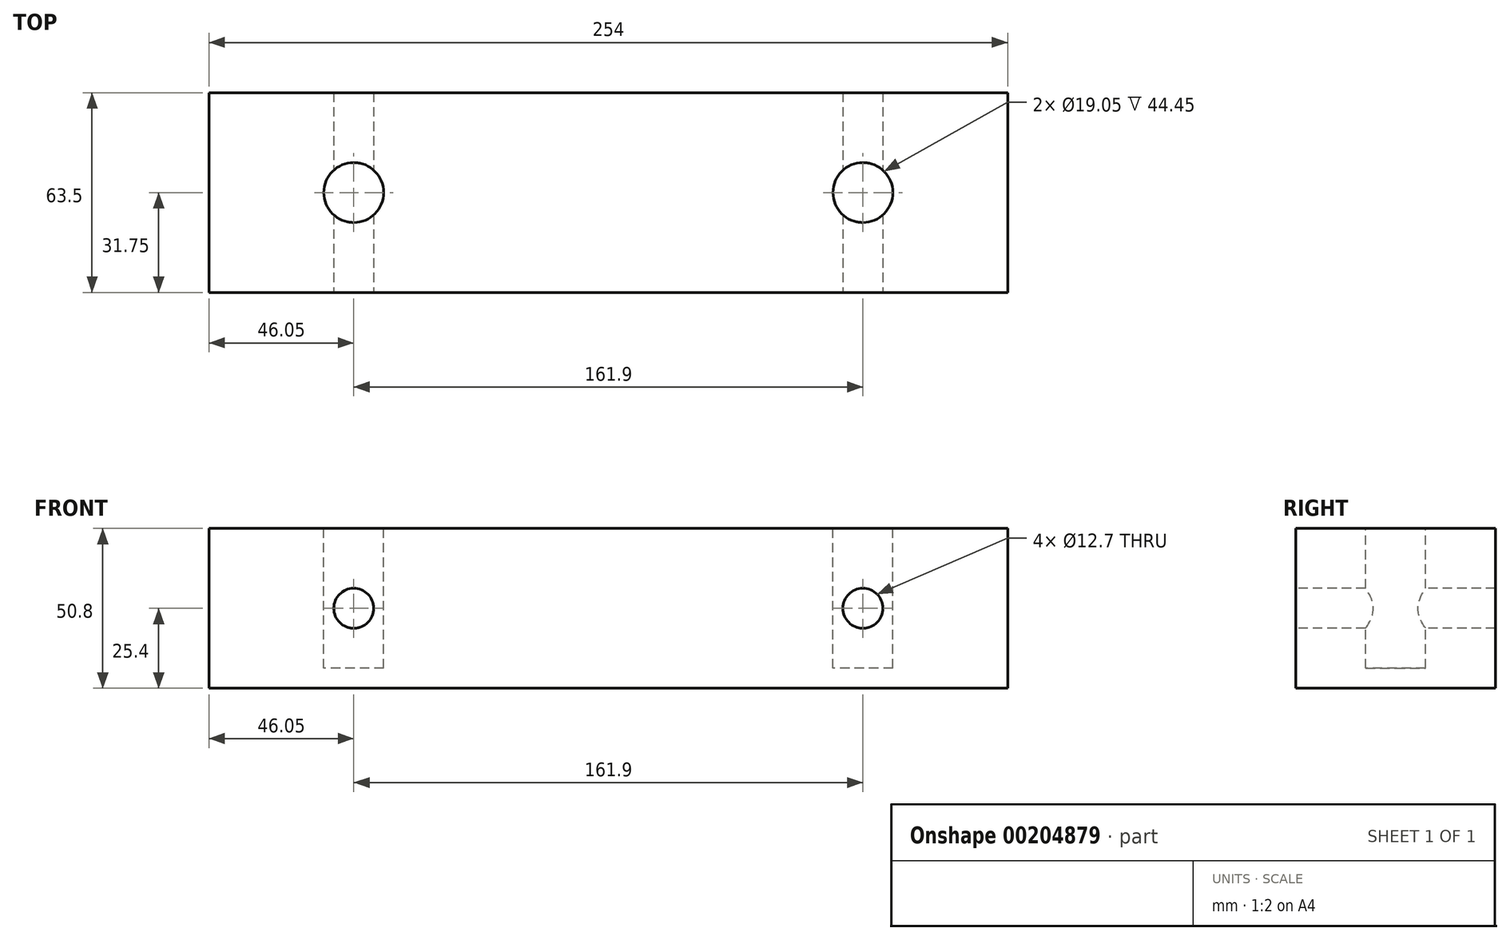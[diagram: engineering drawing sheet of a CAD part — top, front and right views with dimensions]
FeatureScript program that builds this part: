
annotation { "Feature Type Name" : "Feature", "Feature Type Description" : "" }
export const myFeature = defineFeature(function(context is Context, id is Id, definition is map)
    precondition{}
    {
        {
            var Q0;
            Q0=qCreatedBy(makeId("Front.planeOp"),FACE);
            var sketch = newSketch(context, id + "F0", { "sketchPlane" : qUnion([Q0])});
            skLineSegment(sketch, "E0.bottom", {"start": v(-127, -25.4) * mm, "end": v(127, -25.4) * mm});
            skLineSegment(sketch, "E0.top", {"start": v(-127, 25.4) * mm, "end": v(127, 25.4) * mm});
            skLineSegment(sketch, "E0.left", {"start": v(-127, -25.4) * mm, "end": v(-127, 25.4) * mm});
            skLineSegment(sketch, "E0.right", {"start": v(127, -25.4) * mm, "end": v(127, 25.4) * mm});
            skSolve(sketch);
        }
        {
            var Q0;
            Q0=makeQuery(id+"F0.imprint","IMPRINT",FACE,{"disambiguationData":[TD([[makeQuery(id+"F0.imprint","IMPRINT",EDGE,{"derivedFrom":sQuery(id+"F0.wireOp",EDGE,"E0.bottom")}),1.0]])]});
            extrude(context, id + "F1", {"entities" : qUnion([Q0]), "endBound" : BoundingType.SYMMETRIC, "depth" : 63.5 * mm});
        }
        {
            var Q0;
            Q0=makeQuery(id+"F1.opExtrude","SWEPT_FACE",FACE,{"disambiguationData":[OSD([sQuery(id+"F0.wireOp",EDGE,"E0.top")])]});
            var sketch = newSketch(context, id + "F2", { "sketchPlane" : qUnion([Q0])});
            skCircle(sketch, "E1", {"center": v(-80.95, 0) * mm, "radius": 9.53 * mm});
            skCircle(sketch, "E2", {"center": v(80.95, 0) * mm, "radius": 9.53 * mm});
            skSolve(sketch);
        }
        {
            var Q0;
            Q0 = qSketchRegion(id + "F2", true);
            extrude(context, id + "F3", {"entities" : qUnion([Q0]), "operationType" : NewBodyOperationType.REMOVE, "oppositeDirection" : true, "depth" : 44.45 * mm});
        }
        {
            var Q0;
            Q0=makeQuery(id+"F1.opExtrude","CAP_FACE",FACE,{"disambiguationData":[OSD([sQuery(id+"F0.wireOp",EDGE,"E0.bottom"),sQuery(id+"F0.wireOp",EDGE,"E0.top"),sQuery(id+"F0.wireOp",EDGE,"E0.left"),sQuery(id+"F0.wireOp",EDGE,"E0.right")])],"isStart":false});
            var sketch = newSketch(context, id + "F4", { "sketchPlane" : qUnion([Q0])});
            skCircle(sketch, "E3", {"center": v(-80.95, 0) * mm, "radius": 6.35 * mm});
            skCircle(sketch, "E4", {"center": v(80.95, 0) * mm, "radius": 6.35 * mm});
            skSolve(sketch);
        }
        {
            var Q0;
            Q0 = qSketchRegion(id + "F4", true);
            extrude(context, id + "F5", {"entities" : qUnion([Q0]), "operationType" : NewBodyOperationType.REMOVE, "endBound" : BoundingType.THROUGH_ALL, "oppositeDirection" : true, "depth" : 25.4 * mm});
        }
    });
